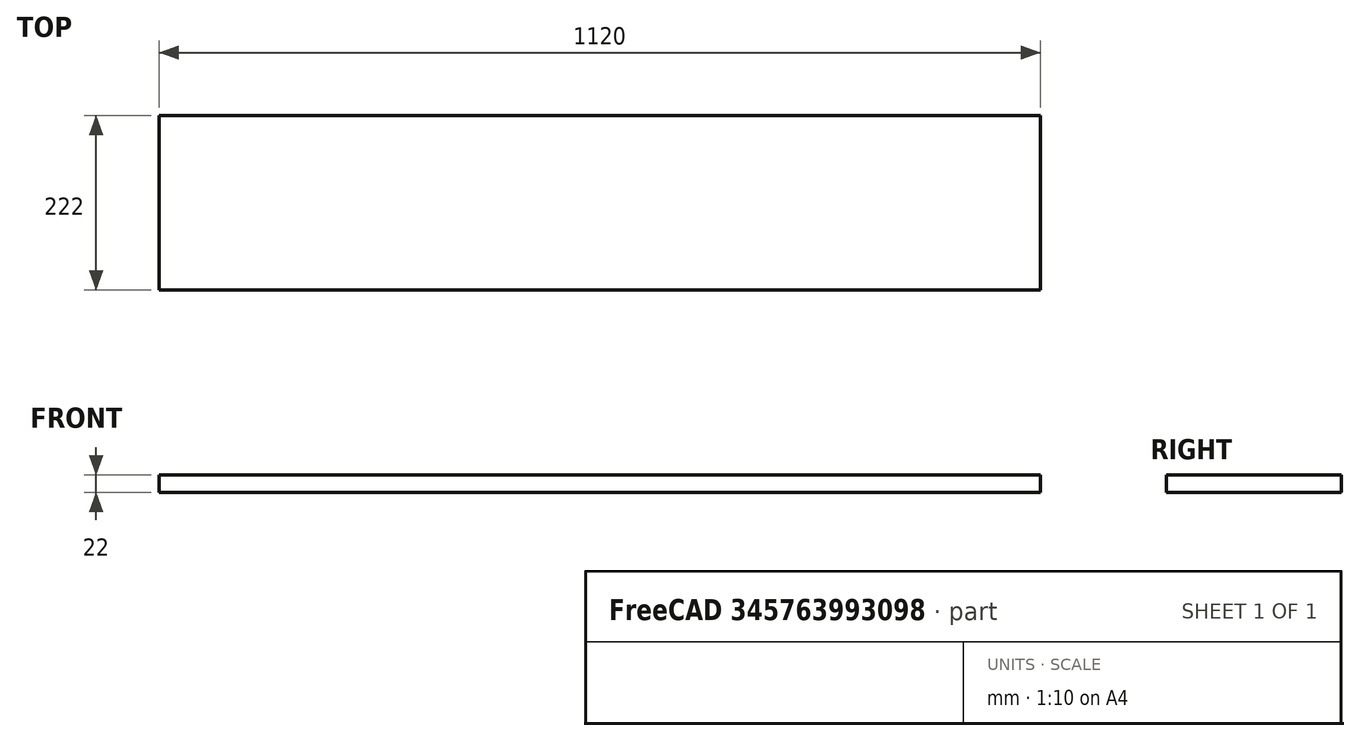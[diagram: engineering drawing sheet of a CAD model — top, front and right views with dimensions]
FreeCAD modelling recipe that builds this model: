
FCSTD DOCUMENT  (FreeCAD 0.20R29603 (Git))
Label: SupportPedaleExpression
License: Public Domain
LicenseURL: http://en.wikipedia.org/wiki/Public_domain
objects: Sketcher::SketchObject×1, PartDesign::Pad×1, PartDesign::Body×1
note: 4 computed .brp shape members not serialized (recipe doc carries the construction recipe); baked Part::Feature solids carry a one-line shape summary decoded from their .brp

FEATURE [Sketcher::SketchObject] Sketch
  FullyConstrained = true
  MapMode = 5
  Support = -> [XY_Plane]
  sketch-geometry (4):
    g0: LineSegment StartX=0 StartY=222 StartZ=0 EndX=1120 EndY=222 EndZ=0
    g1: LineSegment StartX=1120 StartY=222 StartZ=0 EndX=1120 EndY=0 EndZ=0
    g2: LineSegment StartX=1120 StartY=0 StartZ=0 EndX=0 EndY=0 EndZ=0
    g3: LineSegment StartX=0 StartY=0 StartZ=0 EndX=0 EndY=222 EndZ=0
  constraints (11):
    c: Coincident(g0,g1)
    c: Coincident(g1,g2)
    c: Coincident(g2,g3)
    c: Coincident(g3,g0)
    c: Horizontal(g0)
    c: Horizontal(g2)
    c: Vertical(g1)
    c: Vertical(g3)
    c: DistanceX(g0,g0) = 1120
    c: DistanceY(g1,g1) = 222
    c: Coincident(g2,g-1)
FEATURE [PartDesign::Pad] Pad
  Direction = (0,0,1)
  Length = 22
  Length2 = 10
  Profile = -> Sketch
  ReferenceAxis = -> Sketch [N_Axis]
  Type = 0
FEATURE [PartDesign::Body] Body
  Group = -> [Sketch,Pad]
  Origin = -> Origin
  Tip = -> Pad
